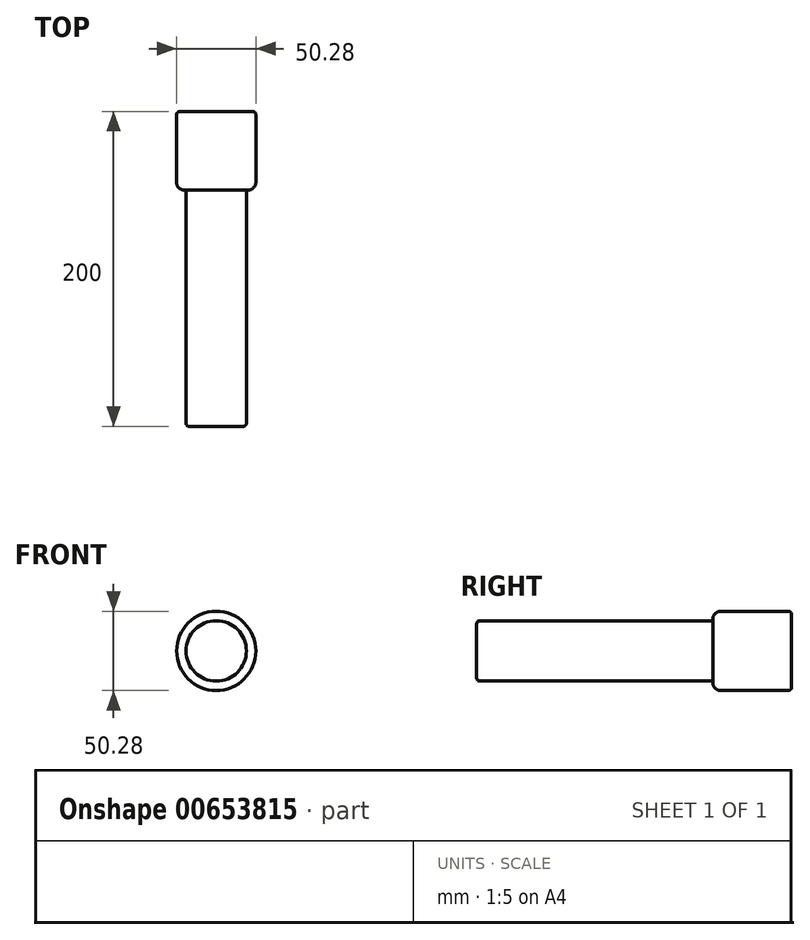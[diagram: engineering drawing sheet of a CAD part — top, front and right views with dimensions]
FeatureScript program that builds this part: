
annotation { "Feature Type Name" : "Feature", "Feature Type Description" : "" }
export const myFeature = defineFeature(function(context is Context, id is Id, definition is map)
    precondition{}
    {
        {
            var Q0;
            Q0=qCreatedBy(makeId("Front.planeOp"),FACE);
            var sketch = newSketch(context, id + "F0", { "sketchPlane" : qUnion([Q0])});
            skCircle(sketch, "E0", {"center": v(0, 0) * mm, "radius": 25.14 * mm});
            skSolve(sketch);
        }
        {
            var Q0;
            Q0 = qSketchRegion(id + "F0", true);
            extrude(context, id + "F1", {"entities" : qUnion([Q0]), "depth" : 50 * mm, "offsetDistance" : 25 * mm});
        }
        {
            var Q0;
            Q0=makeQuery(id+"F1.opExtrude","CAP_FACE",FACE,{"disambiguationData":[OSD([sQuery(id+"F0.wireOp",EDGE,"E0")])],"isStart":false});
            var sketch = newSketch(context, id + "F2", { "sketchPlane" : qUnion([Q0])});
            skCircle(sketch, "E1", {"center": v(0, 0) * mm, "radius": 19.2 * mm});
            skSolve(sketch);
        }
        {
            var Q0;
            Q0 = qSketchRegion(id + "F2", true);
            extrude(context, id + "F3", {"entities" : qUnion([Q0]), "operationType" : NewBodyOperationType.ADD, "depth" : 150 * mm, "offsetDistance" : 25 * mm});
        }
        {
            var Q0;
            Q0=makeQuery(id+"F3.opExtrude","CAP_EDGE",EDGE,{"disambiguationData":[OSD([sQuery(id+"F2.wireOp",EDGE,"E1")])],"isStart":false});
            var Q1;
            Q1=makeQuery(id+"F1.opExtrude","CAP_EDGE",EDGE,{"disambiguationData":[OSD([sQuery(id+"F0.wireOp",EDGE,"E0")])],"isStart":true});
            fillet(context, id + "F4", {"entities" : qUnion([Q0, Q1]), "radius" : 2 * mm, "tangentPropagation" : true, "allowEdgeOverflow" : false});
        }
        {
            var Q0;
            Q0=makeQuery(id+"F1.opExtrude","CAP_EDGE",EDGE,{"disambiguationData":[OSD([sQuery(id+"F0.wireOp",EDGE,"E0")])],"isStart":false});
            fillet(context, id + "F5", {"entities" : qUnion([Q0]), "radius" : 5 * mm, "tangentPropagation" : true, "allowEdgeOverflow" : false});
        }
    });
